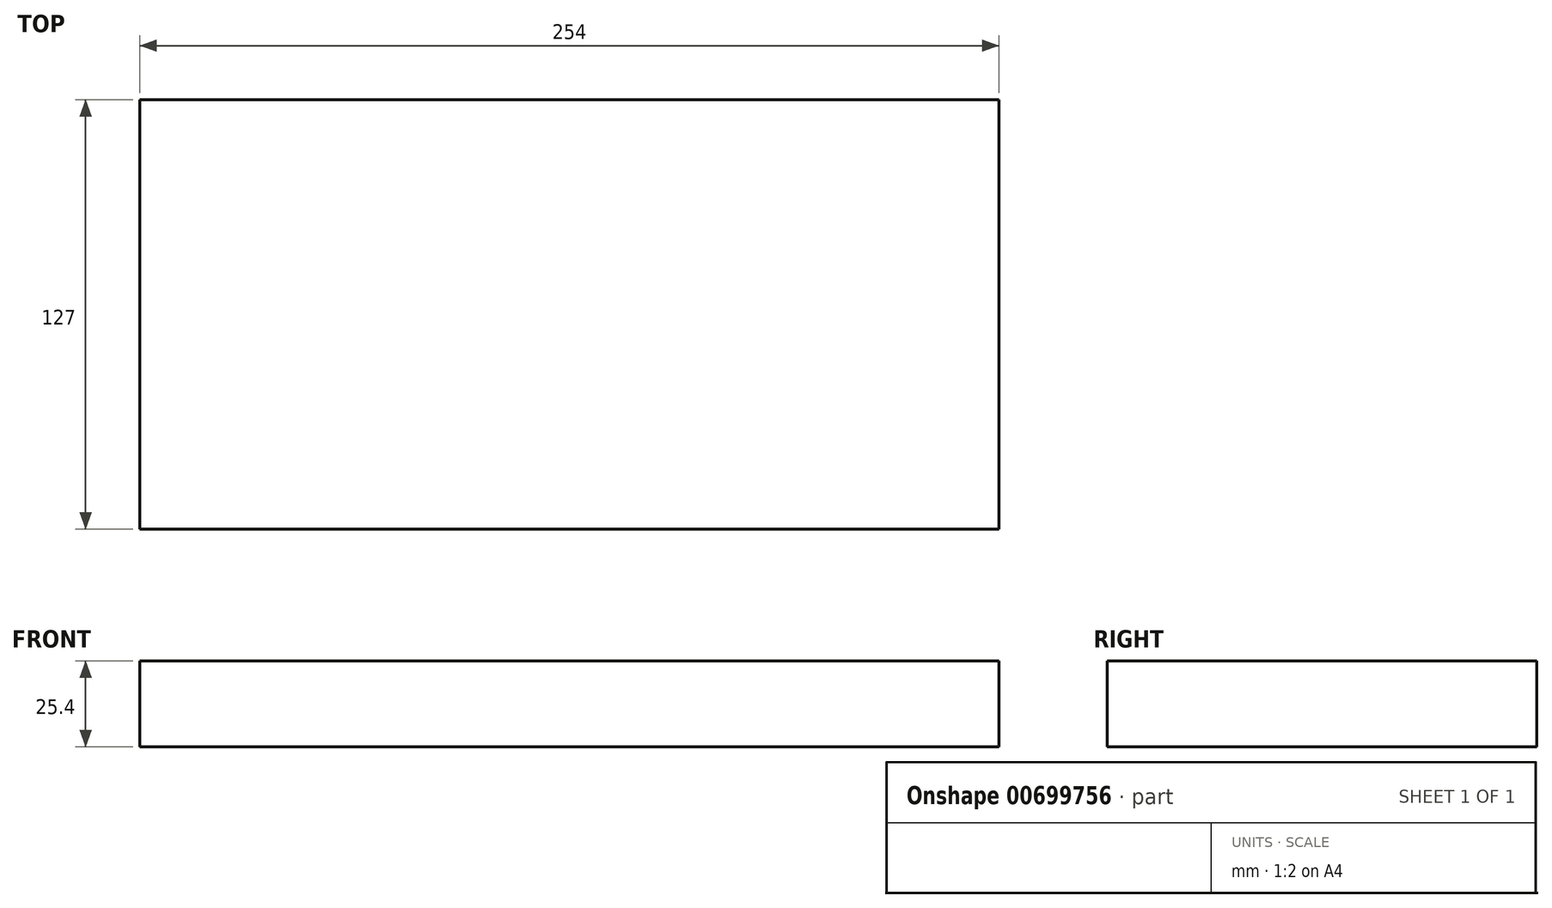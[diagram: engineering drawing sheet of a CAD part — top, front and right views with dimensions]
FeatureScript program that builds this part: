
annotation { "Feature Type Name" : "Feature", "Feature Type Description" : "" }
export const myFeature = defineFeature(function(context is Context, id is Id, definition is map)
    precondition{}
    {
        {
            var Q0;
            Q0=qCreatedBy(makeId("Front.planeOp"),FACE);
            var sketch = newSketch(context, id + "F0", { "sketchPlane" : qUnion([Q0])});
            skLineSegment(sketch, "E0", {"start": v(-93.82, 14.32) * mm, "end": v(-93.82, -11.08) * mm});
            skLineSegment(sketch, "E1", {"start": v(-93.82, -11.08) * mm, "end": v(160.18, -11.08) * mm});
            skLineSegment(sketch, "E2", {"start": v(160.18, -11.08) * mm, "end": v(160.18, 14.32) * mm});
            skLineSegment(sketch, "E3", {"start": v(160.18, 14.32) * mm, "end": v(-93.82, 14.32) * mm});
            skSolve(sketch);
        }
        {
            var Q0;
            Q0 = qSketchRegion(id + "F0", true);
            extrude(context, id + "F1", {"entities" : qUnion([Q0]), "depth" : 127 * mm, "offsetDistance" : 25.4 * mm});
        }
    });
